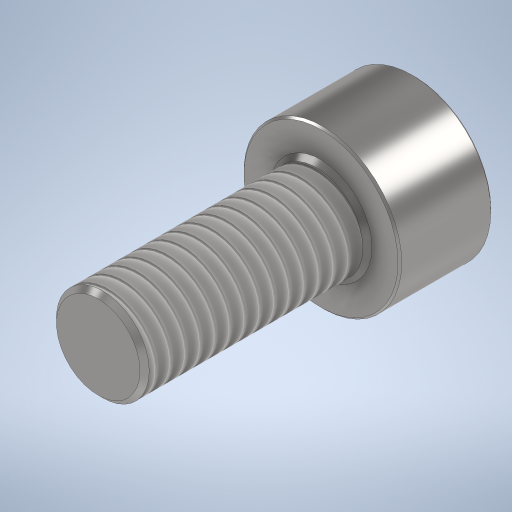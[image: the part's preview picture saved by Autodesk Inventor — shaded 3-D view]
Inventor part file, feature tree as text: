
AUTODESK INVENTOR PART (.ipt)
format: ipt  version: 2024 (Build 280153000, 153)  size: 327,680 bytes
history: native  units: mm
features: extrude x3, chamfer x3, sketch x2, thread x1, hole x1
ambient origin geometry x8: Origin, YZ Plane, XZ Plane, XY Plane, X Axis, Y Axis, Z Axis, Center Point
bodies: Solid1 (feature_tree)
feature tree (10):
  sketch  "Sketch1"  dims[d0=8.5mm d1=5.0mm]
  extrude  "Extrusion1"  Depth=5.0mm
  extrude  "Extrusion2"  Depth=2.5mm TaperAngle=0.0deg
  thread  "Thread1"  [1 undecoded]
  chamfer  "Chamfer1"  Distance=0.1mm Angle=45.0deg
  sketch  "Sketch2"  dims[d2=12.0mm d3=0.0mm d4=5.0mm d5=0.0mm d6=15.0mm d7=0.0mm d8=0.1mm d9=2.0mm d10=45.0deg d11=3.75mm d12=4.0mm d15=0.5mm d16=2.0mm d17=45.0deg d18=3.0mm d19=0.0mm d20=0.25mm d21=2.0mm d22=45.0deg d23=3.75mm d24=6.0mm d25=4.0mm d26=2.0mm d27=90.0deg d28=2.5mm d29=150.0deg]
  hole  "Hole1"  [1 undecoded]
  chamfer  "Chamfer2"  Distance=4.0mm
  extrude  "Extrusion4"  Depth=2.5mm TaperAngle=45.0deg
  chamfer  "Chamfer3"  Distance=3.0mm
note: 2 required parameter values undecoded (feature->parameter linkage not recoverable at this tier; creation-order binding heuristic only, values carry confidence <= 0.55)
